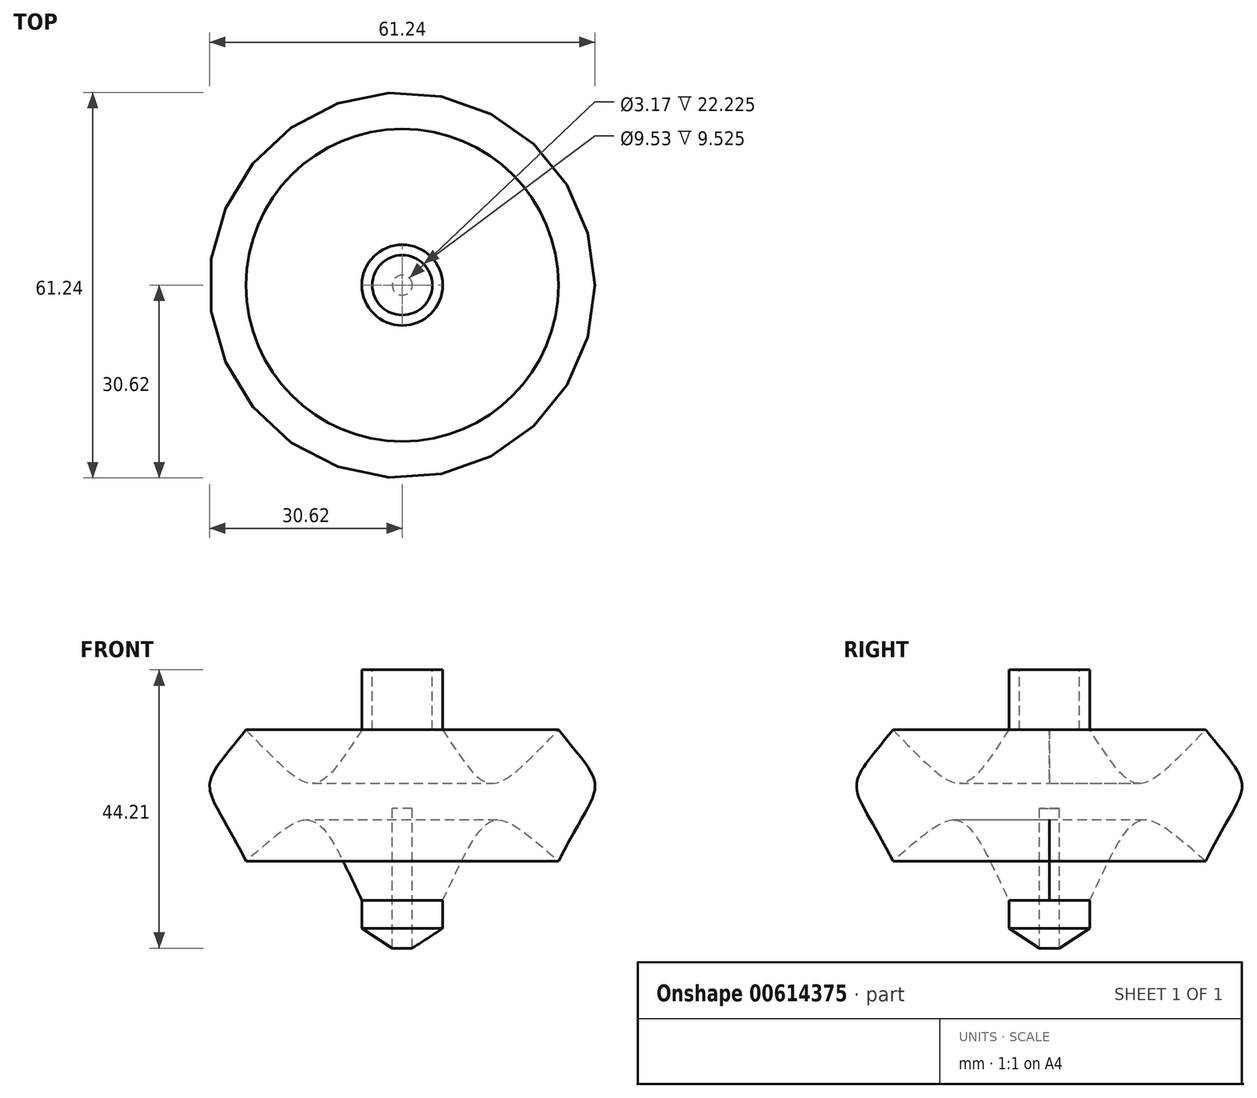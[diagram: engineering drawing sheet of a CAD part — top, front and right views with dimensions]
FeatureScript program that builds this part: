
annotation { "Feature Type Name" : "Feature", "Feature Type Description" : "" }
export const myFeature = defineFeature(function(context is Context, id is Id, definition is map)
    precondition{}
    {
        {
            var Q0;
            Q0=qCreatedBy(makeId("Front.planeOp"),FACE);
            var sketch = newSketch(context, id + "F0", { "sketchPlane" : qUnion([Q0])});
            skLineSegment(sketch, "E0", {"start": v(0, 0) * mm, "end": v(0, 22.23) * mm});
            skLineSegment(sketch, "E1", {"start": v(0, 22.23) * mm, "end": v(1.59, 22.23) * mm});
            skLineSegment(sketch, "E2", {"start": v(1.59, 22.23) * mm, "end": v(1.59, 0) * mm});
            skLineSegment(sketch, "E3", {"start": v(1.59, 0) * mm, "end": v(6.42, 3.14) * mm});
            skLineSegment(sketch, "E4", {"start": v(6.42, 3.14) * mm, "end": v(6.42, 7.6) * mm});
            skLineSegment(sketch, "E5", {"start": v(6.42, 44.21) * mm, "end": v(4.76, 44.21) * mm});
            skLineSegment(sketch, "E6", {"start": v(4.76, 44.21) * mm, "end": v(4.76, 34.69) * mm});
            skLineSegment(sketch, "E7", {"start": v(4.76, 34.69) * mm, "end": v(0, 34.69) * mm});
            skLineSegment(sketch, "E8", {"start": v(0, 34.69) * mm, "end": v(0, 0) * mm});
            skLineSegment(sketch, "E9", {"start": v(6.42, 34.69) * mm, "end": v(6.42, 44.21) * mm});
            skFitSpline(sketch, "E10", {"points": [v(6.42, 34.69) * mm, v(24.82, 34.69) * mm], "startDerivative": vector(22.24, -33.98) * mm, "endDerivative": vector(32.95, 33.98) * mm});
            skFitSpline(sketch, "E11", {"points": [v(6.42, 7.6) * mm, v(24.82, 13.83) * mm], "startDerivative": vector(22.24, 47.28) * mm, "endDerivative": vector(32.95, -28.57) * mm});
            skFitSpline(sketch, "E12", {"points": [v(24.82, 34.69) * mm, v(24.82, 13.83) * mm], "startDerivative": vector(25.5, -31.33) * mm, "endDerivative": vector(-20.8, -40.6) * mm});
            skSolve(sketch);
        }
        {
            var Q0;
            Q0 = qSketchRegion(id + "F0", true);
            var Q1;
            Q1=sQuery(id+"F0.wireOp",EDGE,"E8");
            revolve(context, id + "F1", {"entities" : qUnion([Q0]), "axis" : qUnion([Q1]), "revolveType" : RevolveType.FULL});
        }
    });
